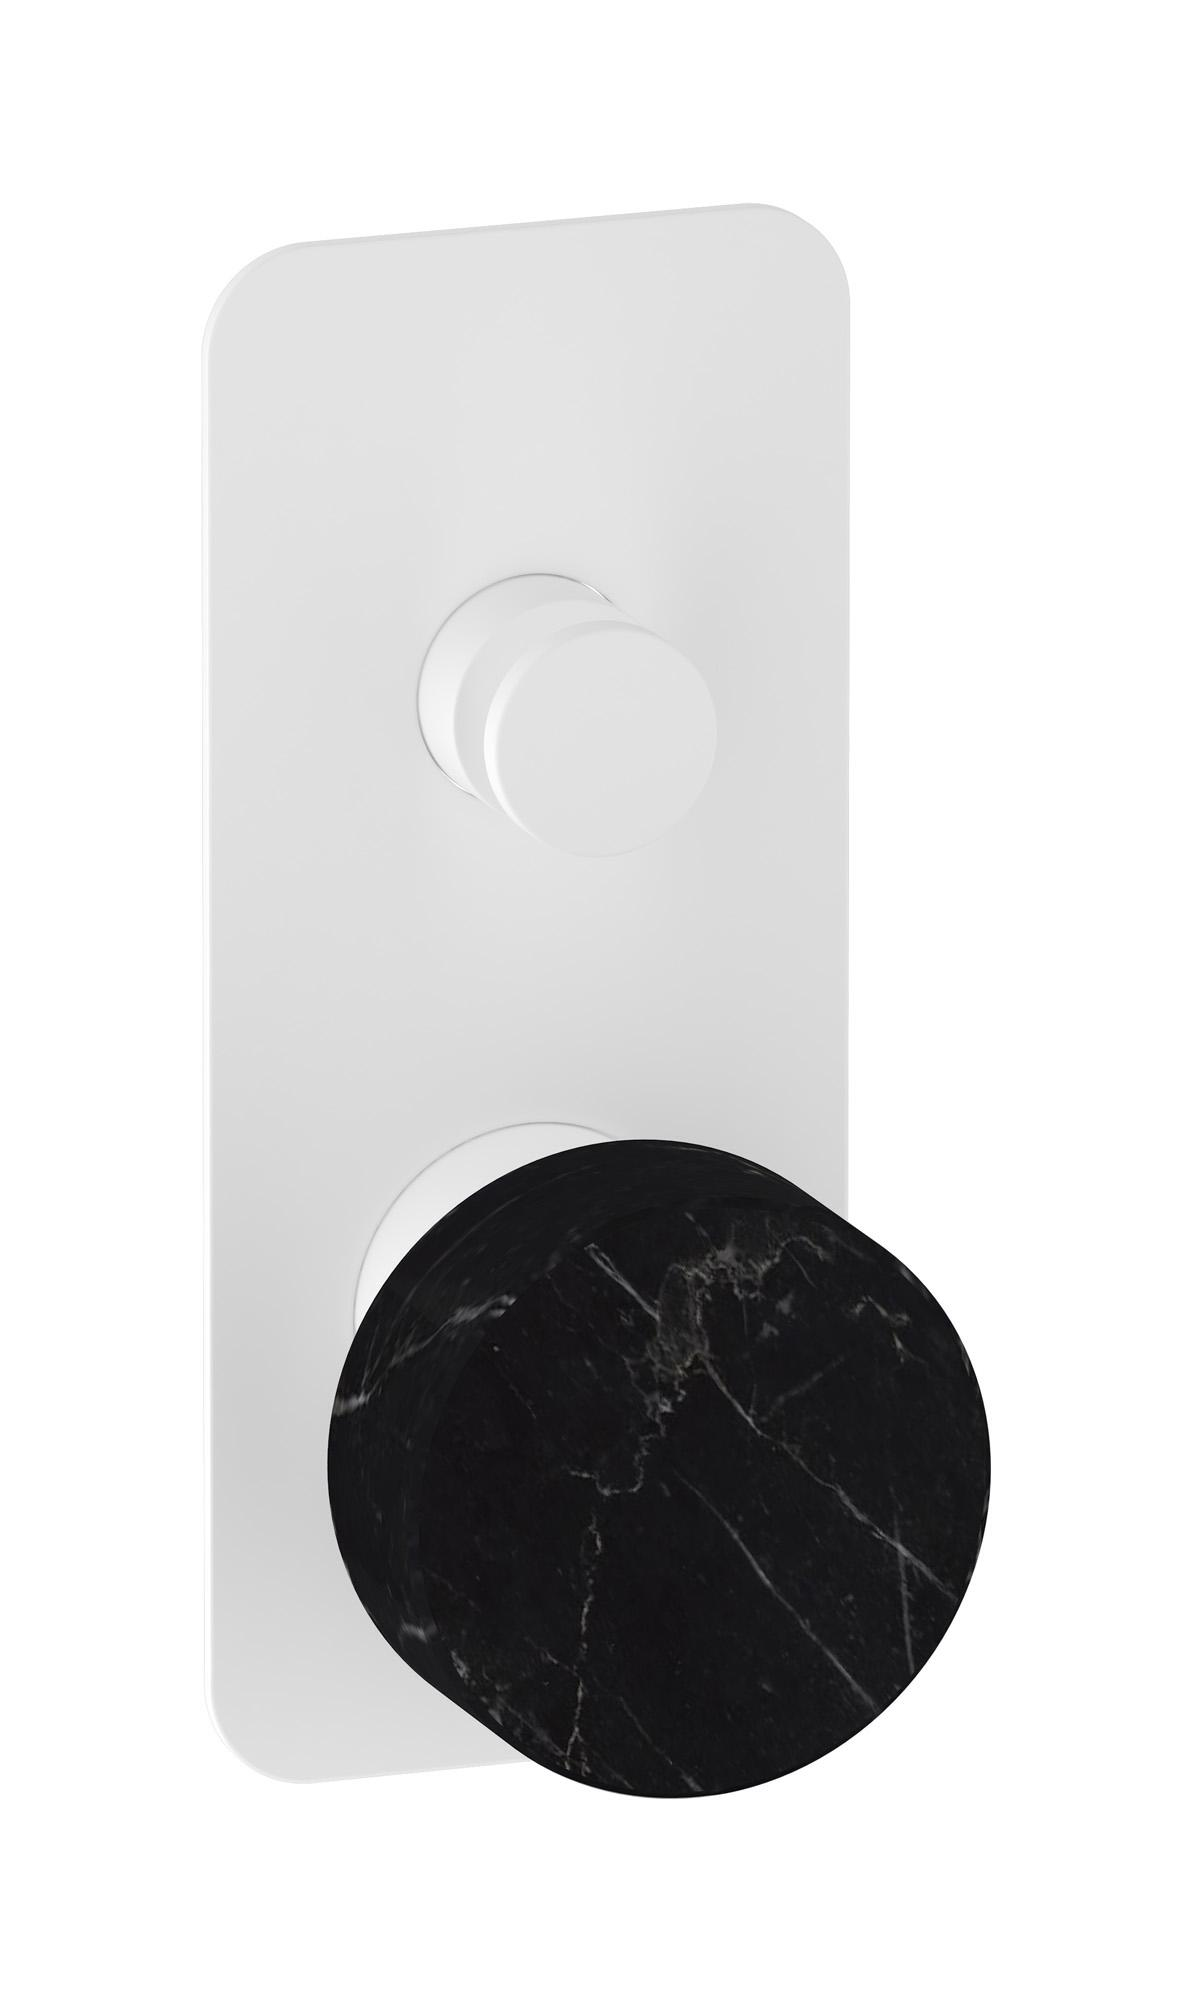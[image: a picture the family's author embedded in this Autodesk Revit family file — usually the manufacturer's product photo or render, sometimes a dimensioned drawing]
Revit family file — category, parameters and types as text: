
# Revit family: MR310_2
name_source: partatom
category: Apparecchi idraulici
units: mm (PartAtom-declared; Revit-internal decimal feet)

## family parameters
Basato su piano di lavoro = No
Condiviso = No
Mantieni orientamento annotazione = No
Numero OmniClass = 23.45.55.17
Punto di calcolo locali = No
Quota connettore circolare = Usa diametro
Sempre verticale = Sì
Taglio con vuoti quando caricato = No
Tipo di parte = Normale
Titolo OmniClass = Mixing Faucets

## types (14) — shared parameters
Cold water inlet = 10 mm  [stored 0.0328084 ft]
Commenti sul tipo = Wall mixer
Connessione CW = No
Connessione HW = No
Connessione di scarico = No
Connessione di ventilazione = No
Descrizione = Exposed parts for manual wall mixer with two ways diverter
Hot water inlet = 10 mm  [stored 0.0328084 ft]
Produttore = IB Rubinetterie S.p.A.
URL = https://www.weareib.it
zero-valued in all types: Prospetto di default

## per-type parameters (varying)
| type | Finishes surface | Immagine tipo | Modello |
| Chrome | IB_Chrome | MR310CC_2.jpg | MR310CC_2 |
| Platinum | IB_Platinum | MR310PL_2.jpg | MR310PL_2 |
| Brushed nickel | IB_Brushed nickel | MR310SS_2.jpg | MR310SS_2 |
| Natural brass | IB_Brass | MR310ON_2.jpg | MR310ON_2 |
| Matt white | IB_matt white | MR310BO_2.jpg | MR310BO_2 |
| Matt black | IB_matt black | MR310NP_2.jpg | MR310NP_2 |
| Black chrome | IB_Black chrome | MR310CF_2.jpg | MR310CF_2 |
| Brushed black chrome | IB_Brushed black chrome | MR310CS_2.jpg | MR310CS_2 |
| Pale gold | IB_Pale gold | MR310II_2.jpg | MR310II_2 |
| Brushed pale gold | IB_brushed pale gold | MR310IS_2.jpg | MR310IS_2 |
| Rose gold | IB_Rose gold | MR310RS_2.jpg | MR310RS_2 |
| Brushed rose gold | IB_Brushed rose gold | MR310SR_2.jpg | MR310SR_2 |
| Gold | IB_gold | MR310OO_2.jpg | MR310OO_2 |
| Brushed gold | IB_brushed gold | MR310OS_2.jpg | MR310OS_2 |

note: [stored X ft] marks values corroborated as IEEE doubles in the binary element streams (Revit-internal decimal feet)
